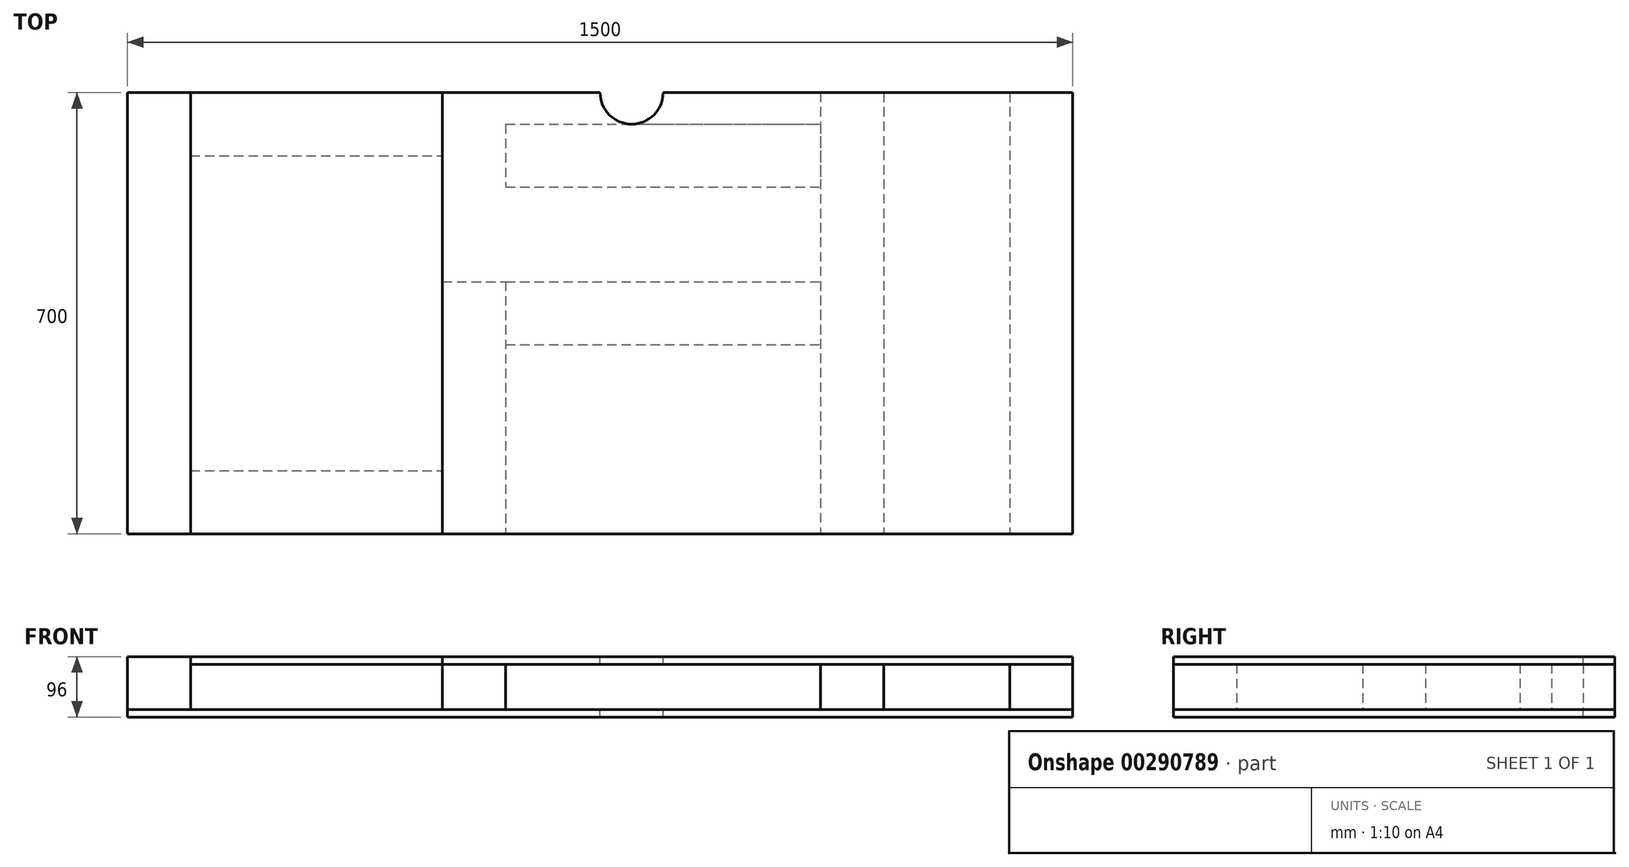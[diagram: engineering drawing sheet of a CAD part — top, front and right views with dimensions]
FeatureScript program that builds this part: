
annotation { "Feature Type Name" : "Feature", "Feature Type Description" : "" }
export const myFeature = defineFeature(function(context is Context, id is Id, definition is map)
    precondition{}
    {
        {
            var Q0;
            Q0=qCreatedBy(makeId("Top.planeOp"),FACE);
            var sketch = newSketch(context, id + "F0", { "sketchPlane" : qUnion([Q0])});
            skLineSegment(sketch, "E0.bottom", {"start": v(0, 0) * mm, "end": v(1500, 0) * mm});
            skLineSegment(sketch, "E0.top", {"start": v(0, -700) * mm, "end": v(1500, -700) * mm});
            skLineSegment(sketch, "E0.left", {"start": v(0, 0) * mm, "end": v(0, -700) * mm});
            skLineSegment(sketch, "E0.right", {"start": v(1500, 0) * mm, "end": v(1500, -700) * mm});
            skSolve(sketch);
        }
        {
            var Q0;
            Q0=makeQuery(id+"F0.imprint","IMPRINT",FACE,{"disambiguationData":[TD([[makeQuery(id+"F0.imprint","IMPRINT",EDGE,{"derivedFrom":sQuery(id+"F0.wireOp",EDGE,"E0.bottom")}),-1.0]])]});
            extrude(context, id + "F1", {"entities" : qUnion([Q0]), "depth" : 12 * mm});
        }
        {
            var Q0;
            Q0=makeQuery(id+"F1.opExtrude","CAP_FACE",FACE,{"disambiguationData":[OSD([sQuery(id+"F0.wireOp",EDGE,"E0.bottom"),sQuery(id+"F0.wireOp",EDGE,"E0.top"),sQuery(id+"F0.wireOp",EDGE,"E0.left"),sQuery(id+"F0.wireOp",EDGE,"E0.right")])],"isStart":false});
            var sketch = newSketch(context, id + "F2", { "sketchPlane" : qUnion([Q0])});
            skLineSegment(sketch, "E1.bottom", {"start": v(0, 0) * mm, "end": v(100, 0) * mm});
            skLineSegment(sketch, "E1.top", {"start": v(0, -700) * mm, "end": v(100, -700) * mm});
            skLineSegment(sketch, "E1.left", {"start": v(0, 0) * mm, "end": v(0, -700) * mm});
            skLineSegment(sketch, "E1.right", {"start": v(100, 0) * mm, "end": v(100, -700) * mm});
            skSolve(sketch);
        }
        {
            var Q0;
            Q0 = qSketchRegion(id + "F2", true);
            extrude(context, id + "F3", {"entities" : qUnion([Q0]), "depth" : 84 * mm});
        }
        {
            var Q0;
            Q0=makeQuery(id+"F1.opExtrude","CAP_FACE",FACE,{"disambiguationData":[OSD([sQuery(id+"F0.wireOp",EDGE,"E0.bottom"),sQuery(id+"F0.wireOp",EDGE,"E0.top"),sQuery(id+"F0.wireOp",EDGE,"E0.left"),sQuery(id+"F0.wireOp",EDGE,"E0.right")])],"isStart":false});
            var sketch = newSketch(context, id + "F4", { "sketchPlane" : qUnion([Q0])});
            skLineSegment(sketch, "E2.bottom", {"start": v(100, 0) * mm, "end": v(500, 0) * mm});
            skLineSegment(sketch, "E2.top", {"start": v(100, -100) * mm, "end": v(500, -100) * mm});
            skLineSegment(sketch, "E2.left", {"start": v(100, 0) * mm, "end": v(100, -100) * mm});
            skLineSegment(sketch, "E2.right", {"start": v(500, 0) * mm, "end": v(500, -100) * mm});
            skSolve(sketch);
        }
        {
            var Q0;
            Q0 = qSketchRegion(id + "F4", true);
            extrude(context, id + "F5", {"entities" : qUnion([Q0]), "depth" : 72 * mm});
        }
        {
            var Q0;
            Q0=makeQuery(id+"F1.opExtrude","CAP_FACE",FACE,{"disambiguationData":[OSD([sQuery(id+"F0.wireOp",EDGE,"E0.bottom"),sQuery(id+"F0.wireOp",EDGE,"E0.top"),sQuery(id+"F0.wireOp",EDGE,"E0.left"),sQuery(id+"F0.wireOp",EDGE,"E0.right")])],"isStart":false});
            var sketch = newSketch(context, id + "F6", { "sketchPlane" : qUnion([Q0])});
            skLineSegment(sketch, "E3.bottom", {"start": v(100, -700) * mm, "end": v(500, -700) * mm});
            skLineSegment(sketch, "E3.top", {"start": v(100, -600) * mm, "end": v(500, -600) * mm});
            skLineSegment(sketch, "E3.left", {"start": v(100, -700) * mm, "end": v(100, -600) * mm});
            skLineSegment(sketch, "E3.right", {"start": v(500, -700) * mm, "end": v(500, -600) * mm});
            skSolve(sketch);
        }
        {
            var Q0;
            Q0 = qSketchRegion(id + "F6", true);
            extrude(context, id + "F7", {"entities" : qUnion([Q0]), "depth" : 72 * mm});
        }
        {
            var Q0;
            Q0=makeQuery(id+"F1.opExtrude","CAP_FACE",FACE,{"disambiguationData":[OSD([sQuery(id+"F0.wireOp",EDGE,"E0.bottom"),sQuery(id+"F0.wireOp",EDGE,"E0.top"),sQuery(id+"F0.wireOp",EDGE,"E0.left"),sQuery(id+"F0.wireOp",EDGE,"E0.right")])],"isStart":false});
            var sketch = newSketch(context, id + "F8", { "sketchPlane" : qUnion([Q0])});
            skLineSegment(sketch, "E4.bottom", {"start": v(1500, 0) * mm, "end": v(1400, 0) * mm});
            skLineSegment(sketch, "E4.top", {"start": v(1500, -700) * mm, "end": v(1400, -700) * mm});
            skLineSegment(sketch, "E4.left", {"start": v(1500, 0) * mm, "end": v(1500, -700) * mm});
            skLineSegment(sketch, "E4.right", {"start": v(1400, 0) * mm, "end": v(1400, -700) * mm});
            skSolve(sketch);
        }
        {
            var Q0;
            Q0 = qSketchRegion(id + "F8", true);
            extrude(context, id + "F9", {"entities" : qUnion([Q0]), "depth" : 72 * mm});
        }
        {
            var Q0;
            Q0=makeQuery(id+"F1.opExtrude","CAP_FACE",FACE,{"disambiguationData":[OSD([sQuery(id+"F0.wireOp",EDGE,"E0.bottom"),sQuery(id+"F0.wireOp",EDGE,"E0.top"),sQuery(id+"F0.wireOp",EDGE,"E0.left"),sQuery(id+"F0.wireOp",EDGE,"E0.right")])],"isStart":false});
            var sketch = newSketch(context, id + "F10", { "sketchPlane" : qUnion([Q0])});
            skLineSegment(sketch, "E5.bottom", {"start": v(1200, 0) * mm, "end": v(1100, 0) * mm});
            skLineSegment(sketch, "E5.top", {"start": v(1200, -700) * mm, "end": v(1100, -700) * mm});
            skLineSegment(sketch, "E5.left", {"start": v(1200, 0) * mm, "end": v(1200, -700) * mm});
            skLineSegment(sketch, "E5.right", {"start": v(1100, 0) * mm, "end": v(1100, -700) * mm});
            skSolve(sketch);
        }
        {
            var Q0;
            Q0=makeQuery(id+"F10.imprint","IMPRINT",FACE,{"disambiguationData":[TD([[makeQuery(id+"F10.imprint","IMPRINT",EDGE,{"derivedFrom":sQuery(id+"F10.wireOp",EDGE,"E5.bottom")}),-1.0]])]});
            extrude(context, id + "F11", {"entities" : qUnion([Q0]), "depth" : 72 * mm});
        }
        {
            var Q0;
            Q0=makeQuery(id+"F1.opExtrude","CAP_FACE",FACE,{"disambiguationData":[OSD([sQuery(id+"F0.wireOp",EDGE,"E0.bottom"),sQuery(id+"F0.wireOp",EDGE,"E0.top"),sQuery(id+"F0.wireOp",EDGE,"E0.left"),sQuery(id+"F0.wireOp",EDGE,"E0.right")])],"isStart":false});
            var sketch = newSketch(context, id + "F12", { "sketchPlane" : qUnion([Q0])});
            skLineSegment(sketch, "E6.bottom", {"start": v(500, -300) * mm, "end": v(600, -300) * mm});
            skLineSegment(sketch, "E6.top", {"start": v(500, -700) * mm, "end": v(600, -700) * mm});
            skLineSegment(sketch, "E6.left", {"start": v(500, -300) * mm, "end": v(500, -700) * mm});
            skLineSegment(sketch, "E6.right", {"start": v(600, -300) * mm, "end": v(600, -700) * mm});
            skSolve(sketch);
        }
        {
            var Q0;
            Q0 = qSketchRegion(id + "F12", true);
            extrude(context, id + "F13", {"entities" : qUnion([Q0]), "depth" : 72 * mm});
        }
        {
            var Q0;
            Q0=makeQuery(id+"F1.opExtrude","CAP_FACE",FACE,{"disambiguationData":[OSD([sQuery(id+"F0.wireOp",EDGE,"E0.bottom"),sQuery(id+"F0.wireOp",EDGE,"E0.top"),sQuery(id+"F0.wireOp",EDGE,"E0.left"),sQuery(id+"F0.wireOp",EDGE,"E0.right")])],"isStart":false});
            var sketch = newSketch(context, id + "F14", { "sketchPlane" : qUnion([Q0])});
            skLineSegment(sketch, "E7.bottom", {"start": v(600, -300) * mm, "end": v(1100, -300) * mm});
            skLineSegment(sketch, "E7.top", {"start": v(600, -400) * mm, "end": v(1100, -400) * mm});
            skLineSegment(sketch, "E7.left", {"start": v(600, -300) * mm, "end": v(600, -400) * mm});
            skLineSegment(sketch, "E7.right", {"start": v(1100, -300) * mm, "end": v(1100, -400) * mm});
            skLineSegment(sketch, "E8.bottom", {"start": v(600, -50) * mm, "end": v(1100, -50) * mm});
            skLineSegment(sketch, "E8.top", {"start": v(600, -150) * mm, "end": v(1100, -150) * mm});
            skLineSegment(sketch, "E8.left", {"start": v(600, -50) * mm, "end": v(600, -150) * mm});
            skLineSegment(sketch, "E8.right", {"start": v(1100, -50) * mm, "end": v(1100, -150) * mm});
            skSolve(sketch);
        }
        {
            var Q0;
            Q0 = qSketchRegion(id + "F14", true);
            extrude(context, id + "F15", {"entities" : qUnion([Q0]), "depth" : 72 * mm});
        }
        {
            var Q0;
            Q0=makeQuery(id+"F13.opExtrude","CAP_FACE",FACE,{"disambiguationData":[OSD([sQuery(id+"F12.wireOp",EDGE,"E6.bottom"),sQuery(id+"F12.wireOp",EDGE,"E6.top"),sQuery(id+"F12.wireOp",EDGE,"E6.left"),sQuery(id+"F12.wireOp",EDGE,"E6.right")])],"isStart":false});
            var sketch = newSketch(context, id + "F16", { "sketchPlane" : qUnion([Q0])});
            skLineSegment(sketch, "E9.bottom", {"start": v(500, 0) * mm, "end": v(1500, 0) * mm});
            skLineSegment(sketch, "E9.top", {"start": v(500, -700) * mm, "end": v(1500, -700) * mm});
            skLineSegment(sketch, "E9.left", {"start": v(500, 0) * mm, "end": v(500, -700) * mm});
            skLineSegment(sketch, "E9.right", {"start": v(1500, 0) * mm, "end": v(1500, -700) * mm});
            skSolve(sketch);
        }
        {
            var Q0;
            Q0 = qSketchRegion(id + "F16", true);
            extrude(context, id + "F17", {"entities" : qUnion([Q0]), "depth" : 12 * mm});
        }
        {
            var Q0;
            Q0=makeQuery(id+"F5.opExtrude","CAP_FACE",FACE,{"disambiguationData":[OSD([sQuery(id+"F4.wireOp",EDGE,"E2.bottom"),sQuery(id+"F4.wireOp",EDGE,"E2.top"),sQuery(id+"F4.wireOp",EDGE,"E2.left"),sQuery(id+"F4.wireOp",EDGE,"E2.right")])],"isStart":false});
            var sketch = newSketch(context, id + "F18", { "sketchPlane" : qUnion([Q0])});
            skLineSegment(sketch, "E10.bottom", {"start": v(100, 0) * mm, "end": v(500, 0) * mm});
            skLineSegment(sketch, "E10.top", {"start": v(100, -700) * mm, "end": v(500, -700) * mm});
            skLineSegment(sketch, "E10.left", {"start": v(100, 0) * mm, "end": v(100, -700) * mm});
            skLineSegment(sketch, "E10.right", {"start": v(500, 0) * mm, "end": v(500, -700) * mm});
            skSolve(sketch);
        }
        {
            var Q0;
            Q0 = qSketchRegion(id + "F18", true);
            extrude(context, id + "F19", {"entities" : qUnion([Q0]), "depth" : 12 * mm});
        }
        {
            var Q0;
            Q0=makeQuery(id+"F17.opExtrude","CAP_FACE",FACE,{"disambiguationData":[OSD([sQuery(id+"F16.wireOp",EDGE,"E9.bottom"),sQuery(id+"F16.wireOp",EDGE,"E9.top"),sQuery(id+"F16.wireOp",EDGE,"E9.left"),sQuery(id+"F16.wireOp",EDGE,"E9.right")])],"isStart":false});
            var sketch = newSketch(context, id + "F20", { "sketchPlane" : qUnion([Q0])});
            skArc(sketch, "E11", {"start": v(750, 0) * mm, "mid": v(800, -50) * mm, "end": v(850, 0) * mm});
            skLineSegment(sketch, "E12", {"start": v(750, 0) * mm, "end": v(850, 0) * mm});
            skSolve(sketch);
        }
        {
            var Q0;
            Q0 = qSketchRegion(id + "F20", true);
            extrude(context, id + "F21", {"entities" : qUnion([Q0]), "operationType" : NewBodyOperationType.REMOVE, "endBound" : BoundingType.THROUGH_ALL, "oppositeDirection" : true, "depth" : 109 * mm});
        }
        {
            var Q0;
            Q0=makeQuery(id+"F1.opExtrude","CAP_FACE",FACE,{"disambiguationData":[OSD([sQuery(id+"F0.wireOp",EDGE,"E0.bottom"),sQuery(id+"F0.wireOp",EDGE,"E0.top"),sQuery(id+"F0.wireOp",EDGE,"E0.left"),sQuery(id+"F0.wireOp",EDGE,"E0.right")])],"isStart":false});
            var sketch = newSketch(context, id + "F22", { "sketchPlane" : qUnion([Q0])});
            skArc(sketch, "E13", {"start": v(750, 0) * mm, "mid": v(800, -50) * mm, "end": v(850, 0) * mm});
            skLineSegment(sketch, "E14", {"start": v(750, 0) * mm, "end": v(850, 0) * mm});
            skSolve(sketch);
        }
        {
            var Q0;
            Q0 = qSketchRegion(id + "F22", true);
            extrude(context, id + "F23", {"entities" : qUnion([Q0]), "operationType" : NewBodyOperationType.REMOVE, "endBound" : BoundingType.THROUGH_ALL, "oppositeDirection" : true, "depth" : 25 * mm});
        }
    });
